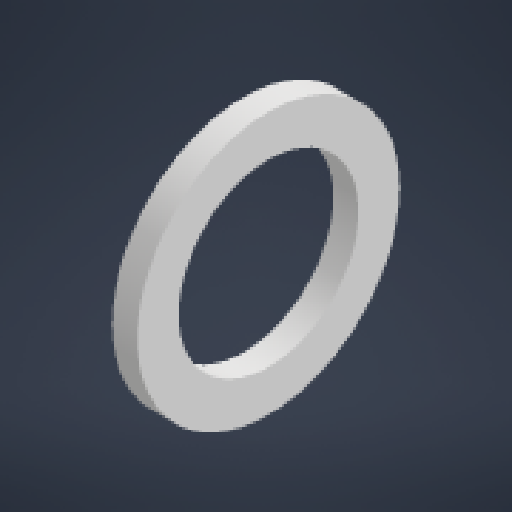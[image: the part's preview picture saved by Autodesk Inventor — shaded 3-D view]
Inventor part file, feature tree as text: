
AUTODESK INVENTOR PART (.ipt)
format: ipt  version: 2024.1 (Build 281209000, 209)  size: 122,368 bytes
history: native  units: in
note: dims shown in document units (in); Inventor stores cm internally (conversion verified against a paired STEP export)
features: extrude x1, sketch x1
ambient origin geometry x8: Origin, YZ Plane, XZ Plane, XY Plane, X Axis, Y Axis, Z Axis, Center Point
bodies: Solid1 (feature_tree)
feature tree (2):
  extrude  "Extrusion1"  Depth=0.048in
  sketch  "Sketch1"  dims[d0=0.3425in d1=0.0787in d2=0.048in d3=0.0in]
